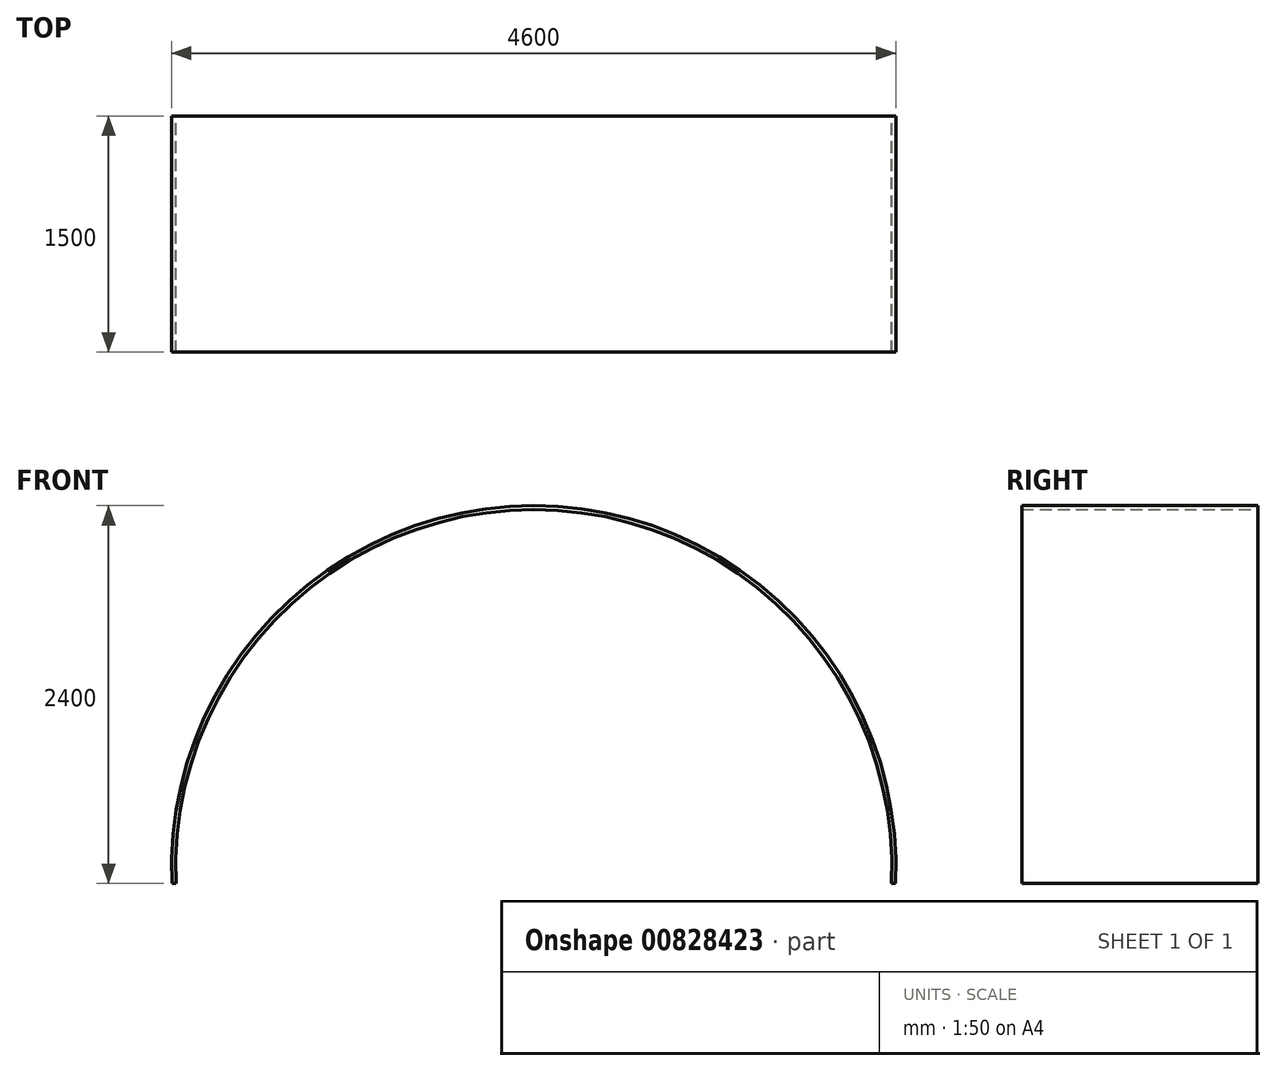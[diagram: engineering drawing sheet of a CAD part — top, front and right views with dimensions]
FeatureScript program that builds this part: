
annotation { "Feature Type Name" : "Feature", "Feature Type Description" : "" }
export const myFeature = defineFeature(function(context is Context, id is Id, definition is map)
    precondition{}
    {
        {
            var Q0;
            Q0=qCreatedBy(makeId("Front.planeOp"),FACE);
            var sketch = newSketch(context, id + "F0", { "sketchPlane" : qUnion([Q0])});
            skArc(sketch, "E0", {"start": v(2297.83, -1178.29) * mm, "mid": v(0, 1221.71) * mm, "end": v(-2297.83, -1178.29) * mm});
            skLineSegment(sketch, "E1", {"start": v(0, 1221.71) * mm, "end": v(-1790.84, 1221.71) * mm, "construction": true});
            skArc(sketch, "E2.0", {"start": v(2272.85, -1177.2) * mm, "mid": v(0, 1196.71) * mm, "end": v(-2272.85, -1177.2) * mm});
            skLineSegment(sketch, "E3", {"start": v(2272.85, -1177.2) * mm, "end": v(2297.83, -1178.29) * mm});
            skLineSegment(sketch, "E4", {"start": v(-2297.83, -1178.29) * mm, "end": v(-2272.85, -1177.2) * mm});
            skSolve(sketch);
        }
        {
            var Q0;
            Q0=makeQuery(id+"F0.imprint","IMPRINT",FACE,{"disambiguationData":[TD([[makeQuery(id+"F0.imprint","IMPRINT",EDGE,{"derivedFrom":sQuery(id+"F0.wireOp",EDGE,"E0")}),1.0]])]});
            extrude(context, id + "F1", {"entities" : qUnion([Q0]), "depth" : 1500 * mm, "offsetDistance" : 25 * mm});
        }
    });
